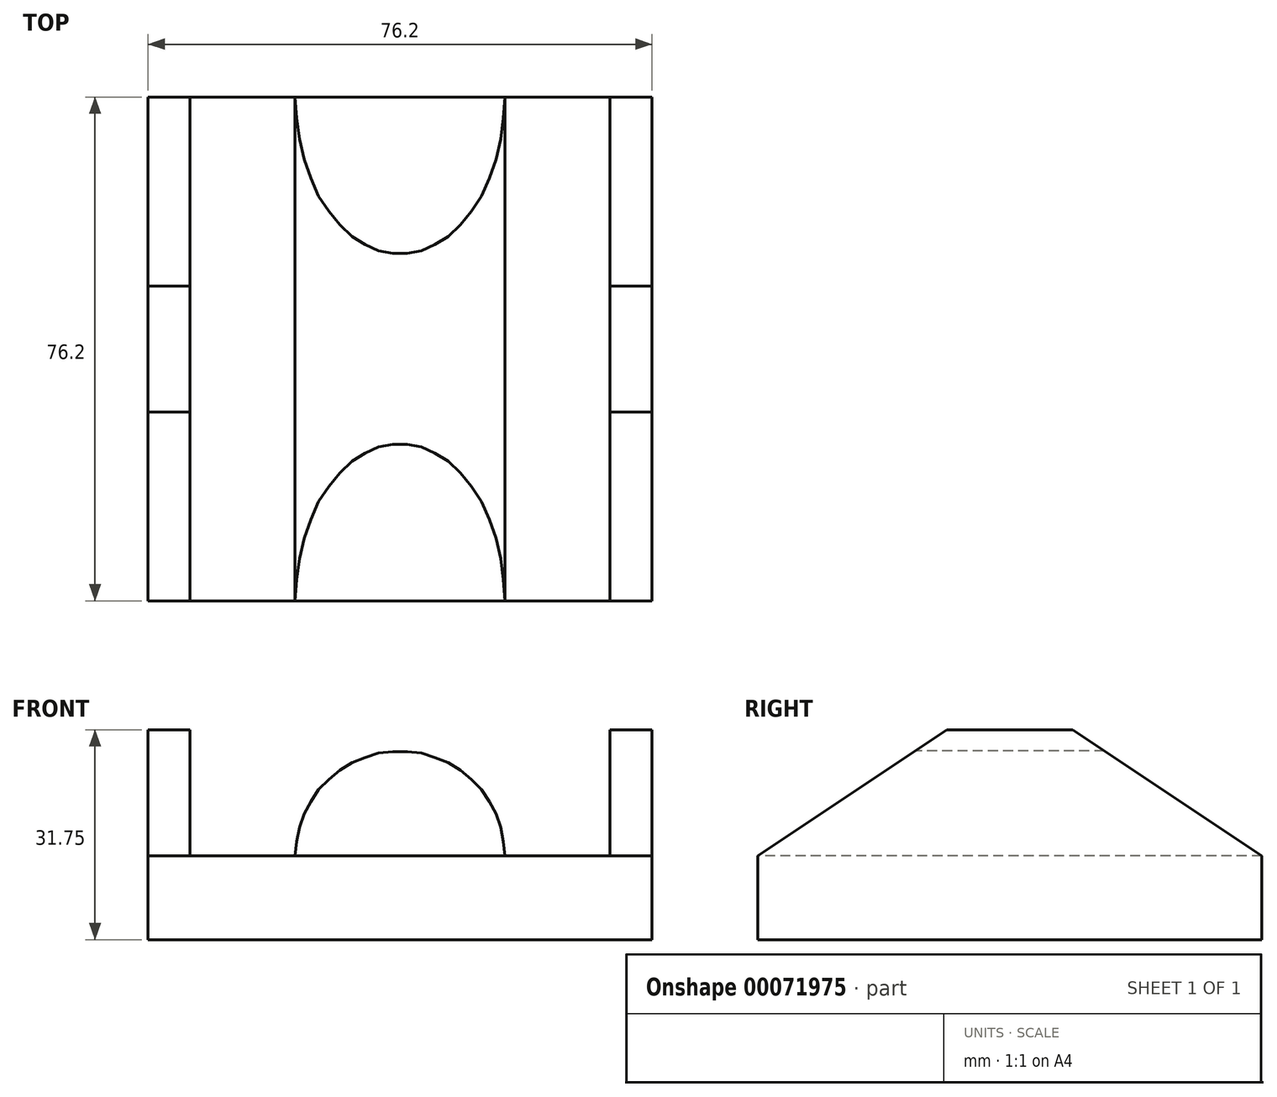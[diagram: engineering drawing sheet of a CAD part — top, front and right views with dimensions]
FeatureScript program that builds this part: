
annotation { "Feature Type Name" : "Feature", "Feature Type Description" : "" }
export const myFeature = defineFeature(function(context is Context, id is Id, definition is map)
    precondition{}
    {
        {
            var Q0;
            Q0=qCreatedBy(makeId("Right.planeOp"),FACE);
            var sketch = newSketch(context, id + "F0", { "sketchPlane" : qUnion([Q0])});
            skLineSegment(sketch, "E0", {"start": v(-38.1, 0) * mm, "end": v(38.1, 0) * mm});
            skLineSegment(sketch, "E1", {"start": v(38.1, 0) * mm, "end": v(38.1, 12.7) * mm});
            skLineSegment(sketch, "E2", {"start": v(38.1, 12.7) * mm, "end": v(9.52, 31.75) * mm});
            skLineSegment(sketch, "E3", {"start": v(9.53, 31.75) * mm, "end": v(-9.53, 31.75) * mm});
            skLineSegment(sketch, "E4", {"start": v(-9.53, 31.75) * mm, "end": v(-38.1, 12.7) * mm});
            skLineSegment(sketch, "E5", {"start": v(-38.1, 12.7) * mm, "end": v(-38.1, 0) * mm});
            skSolve(sketch);
        }
        {
            var Q0;
            Q0=makeQuery(id+"F0.imprint","IMPRINT",FACE,{"disambiguationData":[TD([[makeQuery(id+"F0.imprint","IMPRINT",EDGE,{"derivedFrom":sQuery(id+"F0.wireOp",EDGE,"E0")}),1.0]])]});
            extrude(context, id + "F1", {"entities" : qUnion([Q0]), "depth" : 76.2 * mm});
        }
        {
            var Q0;
            Q0=qCreatedBy(makeId("Front.planeOp"),FACE);
            var sketch = newSketch(context, id + "F2", { "sketchPlane" : qUnion([Q0])});
            skLineSegment(sketch, "E6.bottom", {"start": v(6.35, 31.75) * mm, "end": v(69.85, 31.75) * mm});
            skLineSegment(sketch, "E7", {"start": v(0, 12.7) * mm, "end": v(22.23, 12.7) * mm});
            skArc(sketch, "E8", {"start": v(53.98, 12.7) * mm, "mid": v(38.1, 28.58) * mm, "end": v(22.23, 12.7) * mm});
            skLineSegment(sketch, "E9", {"start": v(69.85, 31.75) * mm, "end": v(69.85, 12.7) * mm});
            skLineSegment(sketch, "E10", {"start": v(6.35, 31.75) * mm, "end": v(6.35, 12.7) * mm});
            skPoint(sketch, "E11.orphan", {"position": v(0, 31.75) * mm});
            skPoint(sketch, "E12.orphan", {"position": v(50.8, 0) * mm});
            skPoint(sketch, "E13.orphan", {"position": v(76.2, 12.7) * mm});
            skLineSegment(sketch, "E14.trimOffspring", {"start": v(53.98, 12.7) * mm, "end": v(69.85, 12.7) * mm});
            skSolve(sketch);
        }
        {
            var Q0;
            Q0 = qSketchRegion(id + "F2", true);
            extrude(context, id + "F3", {"entities" : qUnion([Q0]), "operationType" : NewBodyOperationType.REMOVE, "endBound" : BoundingType.THROUGH_ALL, "oppositeDirection" : true, "depth" : 25.4 * mm, "hasSecondDirection" : true, "secondDirectionBound" : SecondDirectionBoundingType.THROUGH_ALL, "secondDirectionOppositeDirection" : false, "secondDirectionDepth" : 25.4 * mm});
        }
    });
